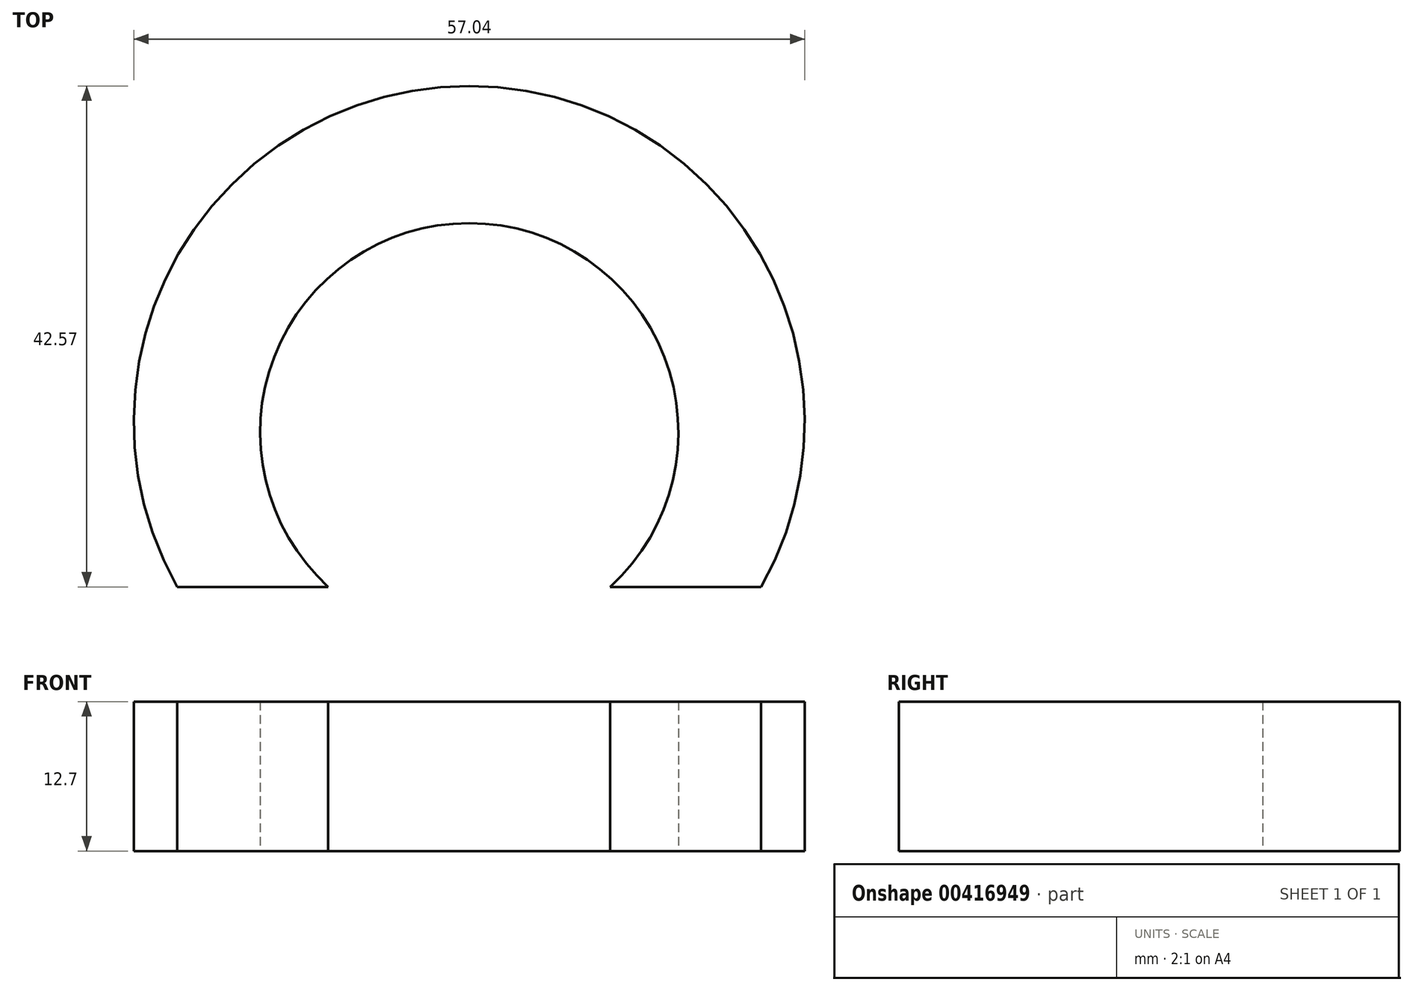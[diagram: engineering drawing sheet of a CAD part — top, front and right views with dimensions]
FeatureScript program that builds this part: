
annotation { "Feature Type Name" : "Feature", "Feature Type Description" : "" }
export const myFeature = defineFeature(function(context is Context, id is Id, definition is map)
    precondition{}
    {
        {
            var Q0;
            Q0=qCreatedBy(makeId("Top.planeOp"),FACE);
            var sketch = newSketch(context, id + "F0", { "sketchPlane" : qUnion([Q0])});
            skLineSegment(sketch, "E0", {"start": v(-54.34, 0) * mm, "end": v(-41.5, 0) * mm});
            skLineSegment(sketch, "E1", {"start": v(-17.54, 0) * mm, "end": v(-4.7, 0) * mm});
            skArc(sketch, "E2", {"start": v(-17.54, 0) * mm, "mid": v(-29.52, 30.91) * mm, "end": v(-41.5, 0) * mm});
            skArc(sketch, "E3", {"start": v(-4.7, 0) * mm, "mid": v(-29.52, 42.57) * mm, "end": v(-54.34, 0) * mm});
            skSolve(sketch);
        }
        {
            var Q0;
            Q0=makeQuery(id+"F0.imprint","IMPRINT",FACE,{"disambiguationData":[TD([[makeQuery(id+"F0.imprint","IMPRINT",EDGE,{"derivedFrom":sQuery(id+"F0.wireOp",EDGE,"E0")}),1.0]])]});
            extrude(context, id + "F1", {"entities" : qUnion([Q0]), "depth" : 12.7 * mm, "offsetDistance" : 25.4 * mm});
        }
    });
